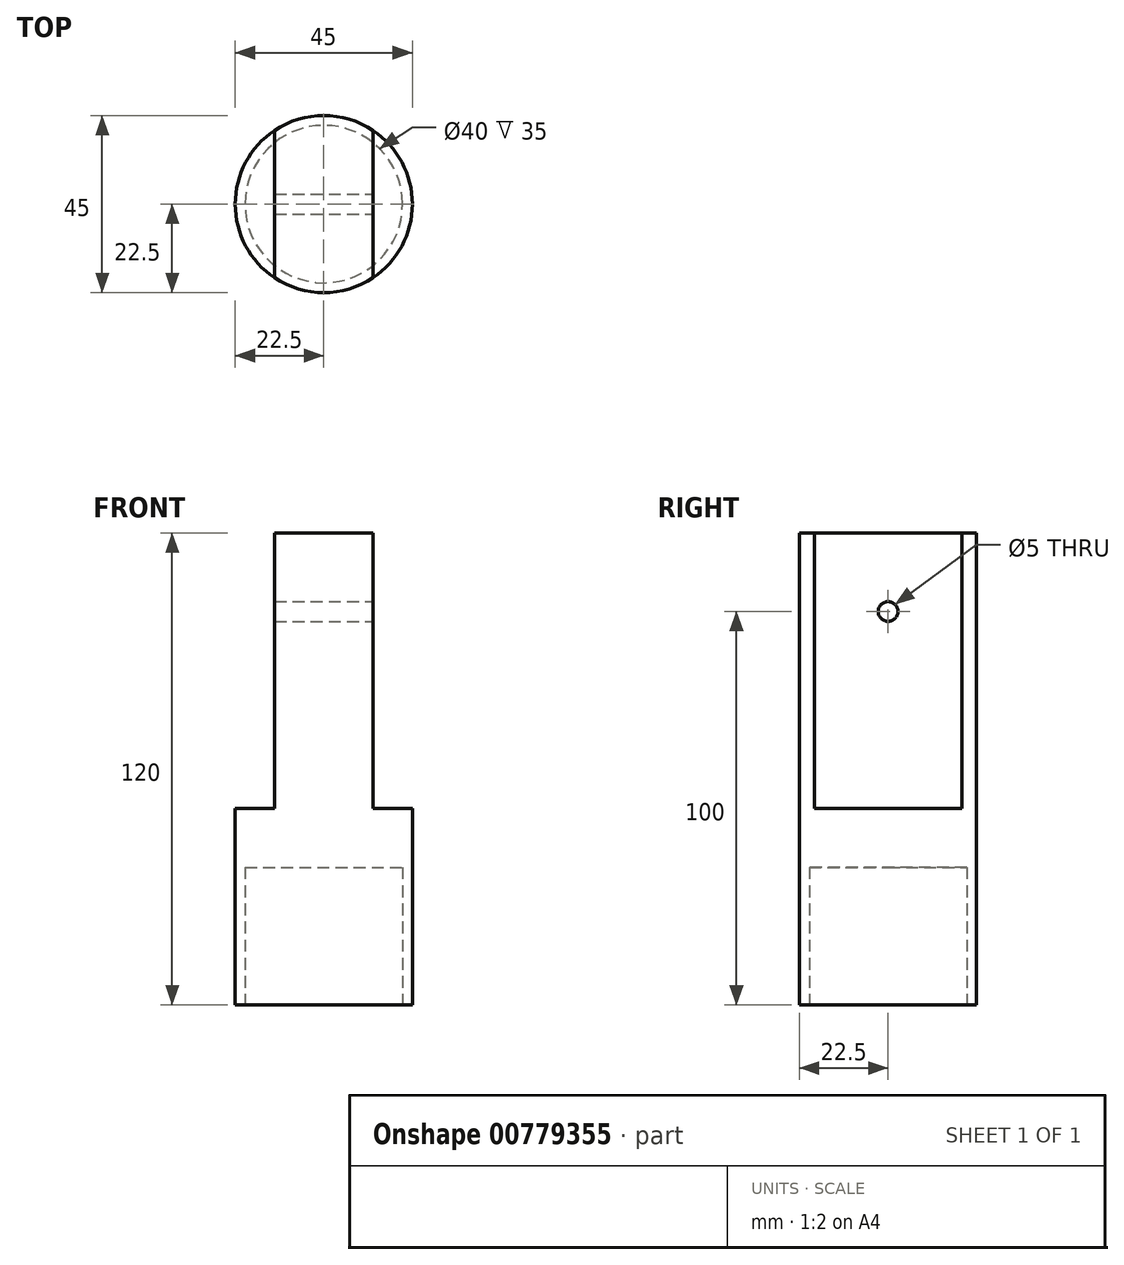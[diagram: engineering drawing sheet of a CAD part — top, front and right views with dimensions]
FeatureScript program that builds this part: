
annotation { "Feature Type Name" : "Feature", "Feature Type Description" : "" }
export const myFeature = defineFeature(function(context is Context, id is Id, definition is map)
    precondition{}
    {
        {
            var Q0;
            Q0=qCreatedBy(makeId("Top.planeOp"),FACE);
            var sketch = newSketch(context, id + "F0", { "sketchPlane" : qUnion([Q0])});
            skCircle(sketch, "E0", {"center": v(0, 0) * mm, "radius": 22.5 * mm});
            skSolve(sketch);
        }
        {
            var Q0;
            Q0=makeQuery(id+"F0.imprint","IMPRINT",FACE,{"disambiguationData":[TD([[makeQuery(id+"F0.imprint","IMPRINT",EDGE,{"derivedFrom":sQuery(id+"F0.wireOp",EDGE,"E0")}),1.0]])]});
            extrude(context, id + "F1", {"entities" : qUnion([Q0]), "flatOperationType" : FlatOperationType.REMOVE, "depth" : 120 * mm, "offsetDistance" : 25 * mm, "domain" : OperationDomain.MODEL});
        }
        {
            var Q0;
            Q0=makeQuery(id+"F1.opExtrude","CAP_FACE",FACE,{"disambiguationData":[OSD([sQuery(id+"F0.wireOp",EDGE,"E0")])],"isStart":false});
            var sketch = newSketch(context, id + "F2", { "sketchPlane" : qUnion([Q0])});
            skLineSegment(sketch, "E1", {"start": v(-12.5, 18.7) * mm, "end": v(-12.5, -18.7) * mm});
            skLineSegment(sketch, "E2", {"start": v(12.5, 18.7) * mm, "end": v(12.5, -18.7) * mm});
            skSolve(sketch);
        }
        {
            var Q0;
            {var subQ0=sQuery(id+"F2.wireOp",EDGE,"E1");Q0=makeQuery(id+"F2.imprint","IMPRINT",FACE,{"disambiguationData":[TD([[makeQuery(id+"F2.imprint","IMPRINT",EDGE,{"derivedFrom":subQ0}),-1.0]])]});}
            var Q1;
            {var subQ0=sQuery(id+"F2.wireOp",EDGE,"E2");Q1=makeQuery(id+"F2.imprint","IMPRINT",FACE,{"disambiguationData":[TD([[makeQuery(id+"F2.imprint","IMPRINT",EDGE,{"derivedFrom":subQ0}),1.0]])]});}
            extrude(context, id + "F3", {"entities" : qUnion([Q0, Q1]), "operationType" : NewBodyOperationType.REMOVE, "flatOperationType" : FlatOperationType.REMOVE, "oppositeDirection" : true, "depth" : 70 * mm, "offsetDistance" : 25 * mm, "domain" : OperationDomain.MODEL});
        }
        {
            var Q0;
            Q0=makeQuery(id+"F1.opExtrude","CAP_FACE",FACE,{"disambiguationData":[OSD([sQuery(id+"F0.wireOp",EDGE,"E0")])],"isStart":true});
            var sketch = newSketch(context, id + "F4", { "sketchPlane" : qUnion([Q0])});
            skCircle(sketch, "E3", {"center": v(0, 0) * mm, "radius": 20 * mm});
            skSolve(sketch);
        }
        {
            var Q0;
            Q0=makeQuery(id+"F4.imprint","IMPRINT",FACE,{"disambiguationData":[TD([[makeQuery(id+"F4.imprint","IMPRINT",EDGE,{"derivedFrom":sQuery(id+"F4.wireOp",EDGE,"E3")}),1.0]])]});
            extrude(context, id + "F5", {"entities" : qUnion([Q0]), "operationType" : NewBodyOperationType.REMOVE, "flatOperationType" : FlatOperationType.REMOVE, "oppositeDirection" : true, "depth" : 35 * mm, "offsetDistance" : 25 * mm, "domain" : OperationDomain.MODEL});
        }
        {
            var Q0;
            Q0=qCreatedBy(makeId("Right.planeOp"),FACE);
            cPlane(context, id + "F6", {"entities" : qUnion([Q0]), "cplaneType" : CPlaneType.OFFSET, "offset" : 22.5 * mm, "width" : 150 * mm, "height" : 150 * mm});
        }
        {
            var Q0;
            Q0=qCreatedBy(id+"F6.planeOp",FACE);
            var sketch = newSketch(context, id + "F7", { "sketchPlane" : qUnion([Q0])});
            skLineSegment(sketch, "E4", {"start": v(-18.7, 100) * mm, "end": v(18.7, 100) * mm});
            skPoint(sketch, "E5", {"position": v(0, 100) * mm});
            skSolve(sketch);
        }
        {
            var Q0;
            Q0=sQuery(id+"F7.wireOp",VERTEX,"E5");
            var Q1;
            Q1=makeQuery(id+"F1.opExtrude","SWEPT_BODY",BODY,{"disambiguationData":[OSD([sQuery(id+"F0.wireOp",EDGE,"E0")])]});
            hole(context, id + "F8", {"style" : HoleStyle.SIMPLE, "endStyle" : HoleEndStyle.THROUGH, "holeDiameter" : 5 * mm, "majorDiameter" : 5 * mm, "isTappedThrough" : true, "tappedDepth" : 12 * mm, "tapClearance" : 3, "locations" : qUnion([Q0]), "scope" : qUnion([Q1])});
        }
    });
